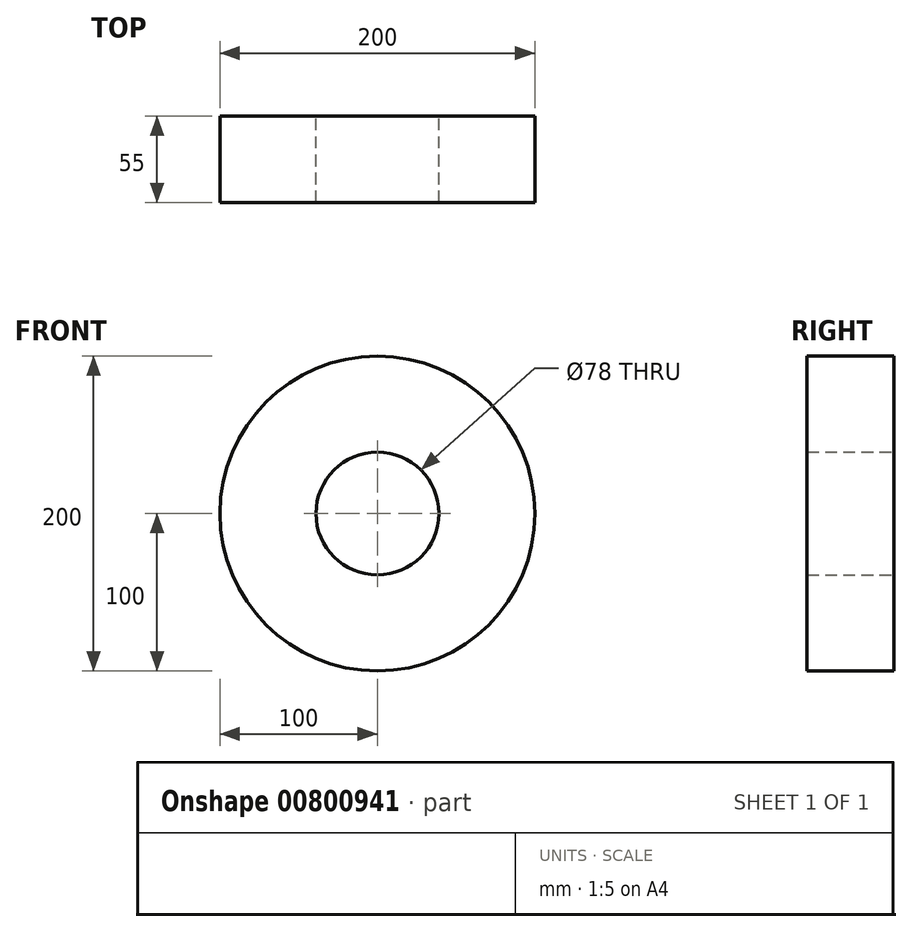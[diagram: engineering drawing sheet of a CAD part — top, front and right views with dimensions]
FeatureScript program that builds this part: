
annotation { "Feature Type Name" : "Feature", "Feature Type Description" : "" }
export const myFeature = defineFeature(function(context is Context, id is Id, definition is map)
    precondition{}
    {
        {
            var Q0;
            Q0=qCreatedBy(makeId("Front.planeOp"),FACE);
            var sketch = newSketch(context, id + "F0", { "sketchPlane" : qUnion([Q0])});
            skCircle(sketch, "E0", {"center": v(0, 0) * mm, "radius": 39 * mm});
            skCircle(sketch, "E1", {"center": v(0, 0) * mm, "radius": 100 * mm});
            skSolve(sketch);
        }
        {
            var Q0;
            Q0 = qSketchRegion(id + "F0", true);
            extrude(context, id + "F1", {"entities" : qUnion([Q0]), "depth" : 55 * mm, "offsetDistance" : 25 * mm});
        }
    });
